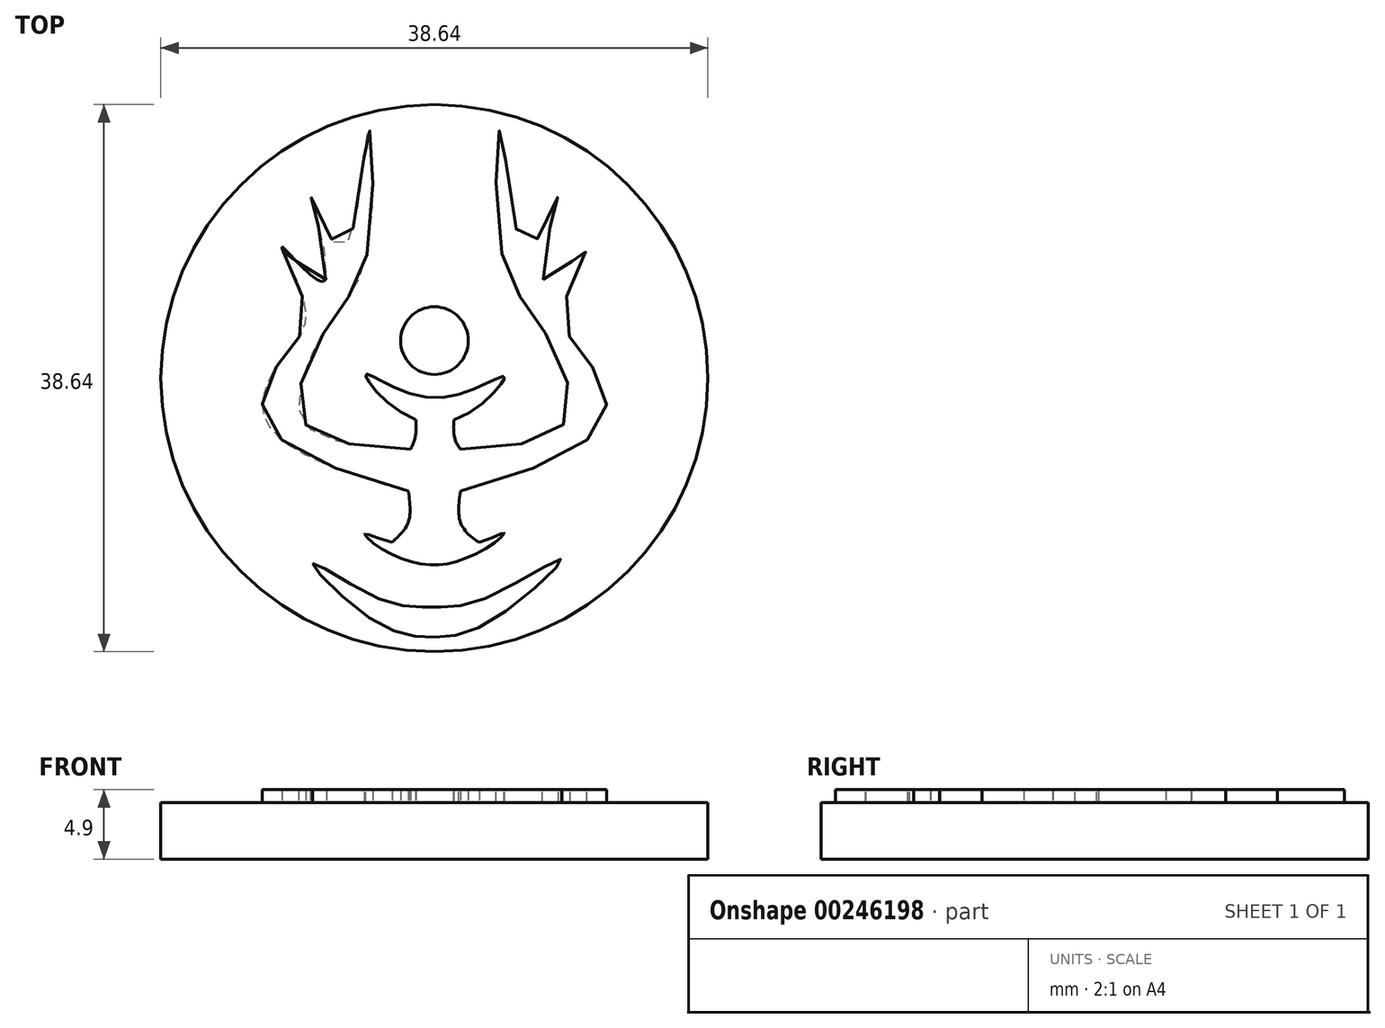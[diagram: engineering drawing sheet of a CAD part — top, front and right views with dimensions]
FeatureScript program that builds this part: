
annotation { "Feature Type Name" : "Feature", "Feature Type Description" : "" }
export const myFeature = defineFeature(function(context is Context, id is Id, definition is map)
    precondition{}
    {
        {
            var Q0;
            Q0=qCreatedBy(makeId("Top.planeOp"),FACE);
            var sketch = newSketch(context, id + "F0", { "sketchPlane" : qUnion([Q0])});
            skCircle(sketch, "E0", {"center": v(-35.13, -9.24) * mm, "radius": 19.32 * mm});
            skSolve(sketch);
        }
        {
            var Q0;
            Q0=makeQuery(id+"F0.imprint","IMPRINT",FACE,{"disambiguationData":[TD([[makeQuery(id+"F0.imprint","IMPRINT",EDGE,{"derivedFrom":sQuery(id+"F0.wireOp",EDGE,"E0")}),1.0]])]});
            var sketch = newSketch(context, id + "F1", { "sketchPlane" : qUnion([Q0])});
            skCircle(sketch, "E1", {"center": v(-35.12, -6.6) * mm, "radius": 2.4 * mm});
            skFitSpline(sketch, "E2", {"points": [v(-39.99, -8.98) * mm, v(-35.12, -10.63) * mm, v(-30.17, -9.15) * mm, v(-35.12, -12.45) * mm, v(-39.99, -8.98) * mm]});
            skFitSpline(sketch, "E3", {"points": [v(-33.74, -12.2) * mm, v(-33.72, -13.33) * mm, v(-33.27, -14.26) * mm], "startDerivative": vector(-0.26, -2.36) * mm, "endDerivative": vector(1.62, -1.85) * mm});
            skFitSpline(sketch, "E4", {"points": [v(-36.45, -12.17) * mm, v(-36.46, -13.26) * mm, v(-36.81, -14.25) * mm], "startDerivative": vector(0.21, -2.24) * mm, "endDerivative": vector(-1.18, -1.89) * mm});
            skFitSpline(sketch, "E5", {"points": [v(-33.27, -14.26) * mm, v(-25.78, -12.17) * mm, v(-27.62, -5.52) * mm, v(-30.46, 0) * mm, v(-30.41, 8.31) * mm, v(-28.57, 0) * mm, v(-26.36, 3.65) * mm, v(-27.34, -2.36) * mm, v(-24.4, 0) * mm, v(-26, -4.33) * mm, v(-24.28, -8) * mm, v(-23.17, -12.17) * mm, v(-33.27, -17.21) * mm], "startDerivative": vector(101.93, 5.19) * mm, "endDerivative": vector(-125.18, -34.2) * mm});
            skFitSpline(sketch, "E6.MirrorCS", {"points": [v(-36.81, -14.25) * mm, v(-44.46, -12.17) * mm, v(-42.62, -5.52) * mm, v(-39.78, 0) * mm, v(-39.83, 8.31) * mm, v(-41.67, 0) * mm, v(-43.88, 3.65) * mm, v(-42.9, -2.36) * mm, v(-45.84, 0) * mm, v(-44.25, -4.33) * mm, v(-45.96, -8) * mm, v(-47.07, -12.17) * mm, v(-36.97, -17.21) * mm], "startDerivative": vector(-101.93, 5.19) * mm, "endDerivative": vector(125.18, -34.2) * mm});
            skFitSpline(sketch, "E7.MirrorCS", {"points": [v(-36.81, -14.25) * mm, v(-44.46, -12.17) * mm, v(-42.62, -5.52) * mm, v(-39.78, 0) * mm, v(-39.83, 8.31) * mm, v(-41.67, 0) * mm, v(-43.88, 3.65) * mm, v(-42.9, -2.36) * mm, v(-45.84, 0) * mm, v(-44.25, -4.33) * mm, v(-45.96, -8) * mm, v(-47.07, -12.17) * mm, v(-36.97, -17.21) * mm], "startDerivative": vector(-101.93, 5.19) * mm, "endDerivative": vector(125.18, -34.2) * mm});
            skFitSpline(sketch, "E8", {"points": [v(-33.27, -17.21) * mm, v(-33.27, -19.46) * mm, v(-31.96, -20.84) * mm], "startDerivative": vector(-0.8, -4.8) * mm, "endDerivative": vector(3.91, -2.42) * mm});
            skFitSpline(sketch, "E9", {"points": [v(-36.97, -17.21) * mm, v(-36.97, -19.4) * mm, v(-38.12, -20.83) * mm], "startDerivative": vector(0.63, -4.5) * mm, "endDerivative": vector(-2.98, -2.72) * mm});
            skFitSpline(sketch, "E10", {"points": [v(-40.05, -20.26) * mm, v(-38.12, -20.83) * mm, v(-31.96, -20.84) * mm, v(-30.2, -20.18) * mm, v(-30.92, -20.9) * mm, v(-33.27, -22.1) * mm, v(-35.05, -22.43) * mm, v(-37.1, -22.1) * mm, v(-39.34, -20.96) * mm, v(-40.05, -20.26) * mm]});
            skFitSpline(sketch, "E11", {"points": [v(-43.72, -22.32) * mm, v(-39.1, -24.8) * mm, v(-35.37, -25.4) * mm, v(-31.53, -24.8) * mm, v(-26.16, -22.04) * mm, v(-31, -26.3) * mm, v(-35.38, -27.55) * mm, v(-39.53, -26.28) * mm, v(-43.72, -22.32) * mm]});
            skSolve(sketch);
        }
        {
            var Q0;
            Q0 = qSketchRegion(id + "F0", true);
            extrude(context, id + "F2", {"entities" : qUnion([Q0]), "depth" : 4 * mm});
        }
        {
            var Q0;
            Q0 = qSketchRegion(id + "F1", true);
            extrude(context, id + "F3", {"entities" : qUnion([Q0]), "operationType" : NewBodyOperationType.ADD, "depth" : 4.9 * mm});
        }
    });
